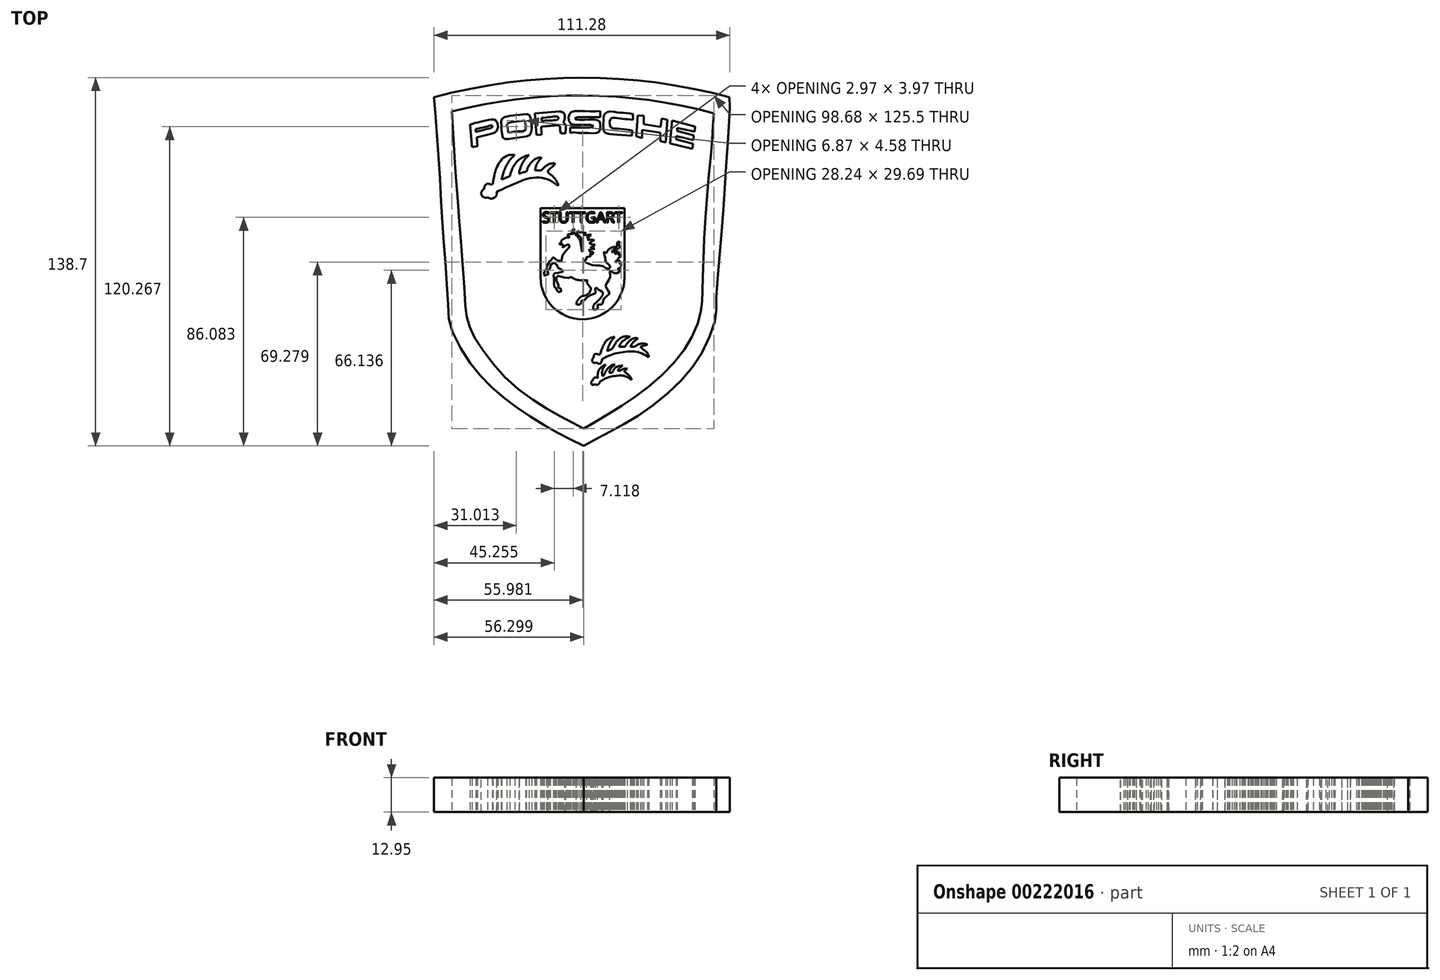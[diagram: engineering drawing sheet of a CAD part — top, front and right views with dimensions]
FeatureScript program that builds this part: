
annotation { "Feature Type Name" : "Feature", "Feature Type Description" : "" }
export const myFeature = defineFeature(function(context is Context, id is Id, definition is map)
    precondition{}
    {
        {
            var Q0;
            Q0=qCreatedBy(makeId("Top.planeOp"),FACE);
            var sketch = newSketch(context, id + "F0", { "sketchPlane" : qUnion([Q0])});
            skFitSpline(sketch, "E0", {"points": [v(35, -72.34) * mm, v(27.57, -68.71) * mm, v(19.8, -64.33) * mm, v(11.03, -58.76) * mm, v(3.44, -53.02) * mm, v(-3.9, -45.93) * mm, v(-10.06, -37.66) * mm, v(-15.16, -27.23) * mm, v(-16.03, -21.12) * mm, v(-16.9, -5.07) * mm, v(-18.13, 10.28) * mm, v(-19.17, 28.25) * mm, v(-20.57, 48.84) * mm, v(-21.37, 59.02) * mm], "startDerivative": vector(-115, 54.33) * mm, "endDerivative": vector(-10.28, 127.52) * mm});
            skArc(sketch, "E1", {"start": v(89.86, 59.02) * mm, "mid": v(34.25, 66.36) * mm, "end": v(-21.37, 59.02) * mm});
            skFitSpline(sketch, "E2", {"points": [v(35, -72.34) * mm, v(45.44, -66.66) * mm, v(56.54, -60.28) * mm, v(70.48, -48.94) * mm, v(79.7, -36.89) * mm, v(84.66, -23.9) * mm, v(84.9, -17.51) * mm, v(86.79, 6.59) * mm, v(88.44, 30.21) * mm, v(89.86, 53.13) * mm, v(89.86, 59.02) * mm], "startDerivative": vector(116.63, 64.03) * mm, "endDerivative": vector(-2, 76.21) * mm});
            skFitSpline(sketch, "E3", {"points": [v(-14.73, 53.62) * mm, v(-13.4, 33.53) * mm, v(-11.42, 6.6) * mm, v(-9.87, -14.37) * mm, v(-9, -24.09) * mm, v(-5.24, -32.92) * mm, v(7.13, -48.15) * mm, v(23.68, -59.85) * mm, v(34.94, -65.81) * mm], "startDerivative": vector(9.08, -141.43) * mm, "endDerivative": vector(98.93, -49.97) * mm});
            skFitSpline(sketch, "E4", {"points": [v(34.94, -65.81) * mm, v(47.97, -58.09) * mm, v(63.64, -46.39) * mm, v(75.56, -31.6) * mm, v(79.32, -20.56) * mm, v(79.76, -13.05) * mm, v(80.64, 11.46) * mm, v(83.07, 40.16) * mm, v(83.95, 52.96) * mm], "startDerivative": vector(107.03, 61.15) * mm, "endDerivative": vector(6.15, 105.05) * mm});
            skArc(sketch, "E5", {"start": v(83.95, 52.96) * mm, "mid": v(34.65, 59.7) * mm, "end": v(-14.73, 53.62) * mm});
            skFitSpline(sketch, "E6.0", {"points": [v(-11.94, 53.8) * mm, v(-11.75, 50.85) * mm, v(-11.47, 46.44) * mm, v(-11.07, 40.3) * mm, v(-10.8, 36.31) * mm, v(-10.57, 33) * mm, v(-10.33, 29.59) * mm, v(-10.02, 25.2) * mm, v(-9.62, 19.8) * mm, v(-9.22, 14.33) * mm, v(-8.8, 8.9) * mm, v(-8.38, 3.58) * mm, v(-7.97, -1.55) * mm, v(-7.6, -6.4) * mm, v(-7.33, -10.14) * mm, v(-7.16, -12.9) * mm, v(-7.05, -14.86) * mm, v(-6.96, -16.65) * mm, v(-6.85, -18.86) * mm, v(-6.7, -20.81) * mm, v(-6.45, -22.57) * mm, v(-6.2, -23.82) * mm, v(-5.87, -25.05) * mm, v(-5.3, -26.7) * mm, v(-4.54, -28.44) * mm, v(-3.52, -30.34) * mm, v(-2.63, -31.86) * mm, v(-1.6, -33.48) * mm, v(-0.08, -35.73) * mm, v(2.1, -38.66) * mm, v(5.1, -42.2) * mm, v(7.85, -45.04) * mm, v(10.16, -47.15) * mm, v(12.56, -49.17) * mm, v(15.67, -51.52) * mm, v(19.45, -54.07) * mm, v(22.56, -55.97) * mm, v(24.95, -57.36) * mm, v(27.25, -58.66) * mm, v(29.98, -60.14) * mm, v(33.12, -61.76) * mm, v(35.17, -62.8) * mm, v(36.2, -63.32) * mm]});
            skArc(sketch, "E6.1", {"start": v(81.03, 50.84) * mm, "mid": v(34.66, 56.9) * mm, "end": v(-11.8, 51.48) * mm});
            skFitSpline(sketch, "E6.2", {"points": [v(33.56, -63.39) * mm, v(35.79, -62.11) * mm, v(39.11, -60.21) * mm, v(43.08, -57.84) * mm, v(45.4, -56.4) * mm, v(47.75, -54.92) * mm, v(50.74, -52.96) * mm, v(54.35, -50.41) * mm, v(57.92, -47.68) * mm, v(60.78, -45.24) * mm, v(62.98, -43.2) * mm, v(65.1, -41.08) * mm, v(67.6, -38.33) * mm, v(70.24, -34.96) * mm, v(72.09, -32.14) * mm, v(73.3, -29.92) * mm, v(74.1, -28.27) * mm, v(74.78, -26.64) * mm, v(75.35, -25.04) * mm, v(75.81, -23.5) * mm, v(76.19, -22.05) * mm, v(76.42, -20.9) * mm, v(76.57, -20.05) * mm, v(76.7, -19.23) * mm, v(76.8, -18.26) * mm, v(76.88, -17.08) * mm, v(76.92, -15.82) * mm, v(76.94, -14.63) * mm, v(76.96, -13.56) * mm, v(76.97, -12.42) * mm, v(77, -10.83) * mm, v(77.03, -8.72) * mm, v(77.1, -5.64) * mm, v(77.23, -1.38) * mm, v(77.44, 4.22) * mm, v(77.7, 9.14) * mm, v(77.95, 13.12) * mm, v(78.23, 17.11) * mm, v(78.63, 22.07) * mm, v(79.14, 27.82) * mm, v(79.56, 32.35) * mm, v(79.87, 35.75) * mm, v(80.1, 38.16) * mm, v(80.3, 40.43) * mm, v(80.46, 42.53) * mm, v(80.61, 44.5) * mm, v(80.79, 46.98) * mm, v(80.97, 49.85) * mm, v(81.1, 52.03) * mm, v(81.16, 53.12) * mm]});
            skLineSegment(sketch, "E7", {"start": v(-9.6, 50.21) * mm, "end": v(-8.62, 38.48) * mm});
            skArc(sketch, "E8", {"start": v(78.46, 49.18) * mm, "mid": v(34.5, 55.61) * mm, "end": v(-9.6, 50.21) * mm});
            skArc(sketch, "E9", {"start": v(77.32, 37.5) * mm, "mid": v(34.41, 43.44) * mm, "end": v(-8.62, 38.48) * mm});
            skLineSegment(sketch, "E10", {"start": v(78.46, 49.18) * mm, "end": v(77.32, 37.5) * mm});
            skLineSegment(sketch, "E11", {"start": v(35.61, 31.18) * mm, "end": v(35.61, 19.11) * mm});
            skLineSegment(sketch, "E12", {"start": v(35.61, 19.11) * mm, "end": v(76.07, 19.11) * mm});
            skLineSegment(sketch, "E13", {"start": v(76.07, 19.11) * mm, "end": v(77.32, 31.18) * mm});
            skLineSegment(sketch, "E14", {"start": v(77.32, 31.18) * mm, "end": v(35.61, 31.18) * mm});
            skLineSegment(sketch, "E15", {"start": v(52.26, 5.93) * mm, "end": v(52.26, -6.08) * mm});
            skLineSegment(sketch, "E16", {"start": v(52.26, -6.08) * mm, "end": v(74.52, -6.08) * mm});
            skLineSegment(sketch, "E17", {"start": v(74.52, -6.08) * mm, "end": v(75.38, 5.93) * mm});
            skLineSegment(sketch, "E18", {"start": v(75.38, 5.93) * mm, "end": v(52.26, 5.93) * mm});
            skFitSpline(sketch, "E19", {"points": [v(0.8, 26.31) * mm, v(1.4, 30.07) * mm, v(3.4, 34.67) * mm, v(6.46, 37.12) * mm, v(9.07, 37.27) * mm], "startDerivative": vector(1.67, 14.46) * mm, "endDerivative": vector(12.44, -1) * mm});
            skFitSpline(sketch, "E20", {"points": [v(9.07, 37.27) * mm, v(6.85, 34.9) * mm, v(4.93, 31.07) * mm, v(4.09, 28) * mm], "startDerivative": vector(-7.23, -6.64) * mm, "endDerivative": vector(-2.15, -9.34) * mm});
            skFitSpline(sketch, "E21", {"points": [v(4.09, 28) * mm, v(7.23, 29.3) * mm], "startDerivative": vector(3.14, 1.3) * mm, "endDerivative": vector(3.14, 1.3) * mm});
            skFitSpline(sketch, "E22", {"points": [v(7.23, 29.3) * mm, v(8.46, 32.83) * mm, v(11.3, 35.97) * mm, v(14.43, 37.27) * mm], "startDerivative": vector(2.7, 10.77) * mm, "endDerivative": vector(10.14, 3.02) * mm});
            skFitSpline(sketch, "E23", {"points": [v(14.43, 37.27) * mm, v(12.29, 34.82) * mm, v(10.76, 31.07) * mm, v(10.76, 30.15) * mm], "startDerivative": vector(-5.9, -5.48) * mm, "endDerivative": vector(0.55, -3.7) * mm});
            skFitSpline(sketch, "E24", {"points": [v(10.76, 30.15) * mm, v(12.36, 30.76) * mm, v(13.44, 30.91) * mm], "startDerivative": vector(3.01, 1.3) * mm, "endDerivative": vector(2.32, 0.18) * mm});
            skFitSpline(sketch, "E25", {"points": [v(13.44, 30.91) * mm, v(14.43, 33.37) * mm, v(17.35, 36.05) * mm, v(19.1, 36.2) * mm], "startDerivative": vector(1.95, 7.2) * mm, "endDerivative": vector(6.15, -0.71) * mm});
            skFitSpline(sketch, "E26", {"points": [v(19.1, 36.2) * mm, v(17.8, 34.67) * mm, v(16.96, 32.83) * mm, v(16.7, 31.46) * mm], "startDerivative": vector(-3.94, -4.08) * mm, "endDerivative": vector(-0.64, -4.47) * mm});
            skFitSpline(sketch, "E27", {"points": [v(16.7, 31.46) * mm, v(19.1, 31.46) * mm], "startDerivative": vector(2.42, 0) * mm, "endDerivative": vector(2.42, 0) * mm});
            skFitSpline(sketch, "E28", {"points": [v(19.1, 31.46) * mm, v(20.67, 33.08) * mm, v(22.43, 33.96) * mm, v(24.35, 34.01) * mm], "startDerivative": vector(4.24, 4.99) * mm, "endDerivative": vector(6.01, -0.4) * mm});
            skFitSpline(sketch, "E29", {"points": [v(24.35, 34.01) * mm, v(22.58, 32.3) * mm, v(21.5, 30.91) * mm, v(23.22, 29.3) * mm, v(25.03, 26.9) * mm, v(25.47, 25.58) * mm], "startDerivative": vector(-7.92, -8.09) * mm, "endDerivative": vector(1.93, -7.65) * mm});
            skFitSpline(sketch, "E30", {"points": [v(25.47, 25.58) * mm, v(22.48, 27.54) * mm, v(19.1, 28.62) * mm, v(14.43, 28.42) * mm, v(9.07, 26.46) * mm, v(4.09, 24.25) * mm, v(2.22, 23.32) * mm], "startDerivative": vector(-18.76, 13.66) * mm, "endDerivative": vector(-13.58, -7.08) * mm});
            skFitSpline(sketch, "E31", {"points": [v(2.22, 23.32) * mm, v(2.22, 22.34) * mm, v(1.49, 21.26) * mm, v(0, 20.82) * mm, v(-1.21, 21.26) * mm], "startDerivative": vector(0.56, -4.4) * mm, "endDerivative": vector(-4.55, 2.43) * mm});
            skFitSpline(sketch, "E32", {"points": [v(-1.21, 21.26) * mm, v(-2.54, 21.26) * mm, v(-3.57, 22.34) * mm, v(-3.37, 23.6) * mm, v(-2.58, 24.45) * mm, v(-2.24, 25.58) * mm, v(-1.21, 26.46) * mm, v(0, 26.16) * mm, v(0.8, 26.31) * mm], "startDerivative": vector(-10.36, -1.82) * mm, "endDerivative": vector(7.37, 2.91) * mm});
            skLineSegment(sketch, "E33", {"start": v(33.17, 19.11) * mm, "end": v(33.17, 41.97) * mm});
            skLineSegment(sketch, "E34", {"start": v(16.5, 19.11) * mm, "end": v(33.17, 19.11) * mm});
            skLineSegment(sketch, "E35", {"start": v(16.5, 19.11) * mm, "end": v(16.5, 17.4) * mm});
            skLineSegment(sketch, "E36", {"start": v(16.5, 14.72) * mm, "end": v(16.5, 7.66) * mm});
            skLineSegment(sketch, "E37", {"start": v(17.06, 6.18) * mm, "end": v(17.06, 4.03) * mm});
            skLineSegment(sketch, "E38", {"start": v(17.06, 4.03) * mm, "end": v(15.66, 4.48) * mm});
            skLineSegment(sketch, "E39", {"start": v(15.66, 4.48) * mm, "end": v(17.06, 6.18) * mm});
            skLineSegment(sketch, "E40", {"start": v(17.06, 1.93) * mm, "end": v(17.06, -6.32) * mm});
            skLineSegment(sketch, "E41", {"start": v(17.06, -6.32) * mm, "end": v(-6.18, -6.32) * mm});
            skLineSegment(sketch, "E42", {"start": v(-6.18, -6.32) * mm, "end": v(-8.79, 36.4) * mm});
            skArc(sketch, "E43", {"start": v(33.17, 41.97) * mm, "mid": v(12.03, 40.4) * mm, "end": v(-8.79, 36.4) * mm});
            skArc(sketch, "E44", {"start": v(-4.38, -19.17) * mm, "mid": v(-3.07, -25.62) * mm, "end": v(0, -31.44) * mm});
            skArc(sketch, "E45", {"start": v(19.45, -19.17) * mm, "mid": v(25.5, -24.57) * mm, "end": v(33.17, -27.26) * mm});
            skLineSegment(sketch, "E46", {"start": v(-4.38, -19.17) * mm, "end": v(19.45, -19.17) * mm});
            skLineSegment(sketch, "E47", {"start": v(0, -31.44) * mm, "end": v(33.17, -31.44) * mm});
            skLineSegment(sketch, "E48", {"start": v(33.17, -31.44) * mm, "end": v(33.17, -27.26) * mm});
            skLineSegment(sketch, "E49", {"start": v(11.01, -44.51) * mm, "end": v(33.27, -44.51) * mm});
            skLineSegment(sketch, "E50", {"start": v(33.27, -44.51) * mm, "end": v(33.27, -59.66) * mm});
            skArc(sketch, "E51", {"start": v(11.01, -44.51) * mm, "mid": v(21.66, -52.8) * mm, "end": v(33.27, -59.66) * mm});
            skLineSegment(sketch, "E52", {"start": v(35.56, -26.74) * mm, "end": v(35.56, -59.86) * mm});
            skArc(sketch, "E53", {"start": v(35.56, -26.74) * mm, "mid": v(39.29, -26.2) * mm, "end": v(42.79, -24.83) * mm});
            skArc(sketch, "E54", {"start": v(45.23, -23.38) * mm, "mid": v(50.72, -16.77) * mm, "end": v(52.26, -8.32) * mm});
            skLineSegment(sketch, "E55", {"start": v(52.26, -8.32) * mm, "end": v(74.52, -8.32) * mm});
            skFitSpline(sketch, "E56", {"points": [v(35.56, -59.86) * mm, v(46.42, -53.55) * mm, v(60.92, -42.5) * mm, v(70.52, -29.8) * mm, v(73.6, -19.66) * mm, v(74.52, -8.32) * mm], "startDerivative": vector(54.2, 29.95) * mm, "endDerivative": vector(3.1, 63.4) * mm});
            skLineSegment(sketch, "E57", {"start": v(18.72, 17.2) * mm, "end": v(50.36, 17.2) * mm});
            skLineSegment(sketch, "E58", {"start": v(18.72, 17.2) * mm, "end": v(18.72, -2.86) * mm});
            skLineSegment(sketch, "E59", {"start": v(50.36, 17.2) * mm, "end": v(50.36, -2.86) * mm});
            skLineSegment(sketch, "E60", {"start": v(18.72, -2.86) * mm, "end": v(18.72, -8.82) * mm});
            skLineSegment(sketch, "E61", {"start": v(50.36, -2.86) * mm, "end": v(50.36, -8.82) * mm});
            skArc(sketch, "E62", {"start": v(18.72, -8.82) * mm, "mid": v(34.54, -24.64) * mm, "end": v(50.36, -8.82) * mm});
            skLineSegment(sketch, "E63", {"start": v(16.5, 17.4) * mm, "end": v(15.06, 17.4) * mm});
            skFitSpline(sketch, "E64", {"points": [v(15.06, 17.4) * mm, v(15.83, 18.96) * mm, v(17.27, 20.5) * mm, v(18.01, 21.29) * mm], "startDerivative": vector(1.78, 4.5) * mm, "endDerivative": vector(2.4, 2.6) * mm});
            skFitSpline(sketch, "E65", {"points": [v(18.01, 21.29) * mm, v(16.42, 21.29) * mm, v(14.13, 19.47) * mm, v(12.9, 17.4) * mm], "startDerivative": vector(-5.47, 1.03) * mm, "endDerivative": vector(-2.9, -6) * mm});
            skFitSpline(sketch, "E66", {"points": [v(12.9, 17.4) * mm, v(10.36, 16.77) * mm], "startDerivative": vector(-2.55, -0.63) * mm, "endDerivative": vector(-2.55, -0.63) * mm});
            skFitSpline(sketch, "E67", {"points": [v(10.36, 16.77) * mm, v(10.73, 18.18) * mm, v(11.95, 20.32) * mm, v(13.87, 22.32) * mm], "startDerivative": vector(0.97, 4.93) * mm, "endDerivative": vector(5.43, 5.06) * mm});
            skFitSpline(sketch, "E68", {"points": [v(13.87, 22.32) * mm, v(12.28, 22.32) * mm, v(9.7, 20.58) * mm, v(7.66, 17.4) * mm, v(7.25, 15.66) * mm], "startDerivative": vector(-7.6, 1.12) * mm, "endDerivative": vector(-1.06, -7.6) * mm});
            skFitSpline(sketch, "E69", {"points": [v(7.25, 15.66) * mm, v(4.5, 14.86) * mm], "startDerivative": vector(-2.76, -0.8) * mm, "endDerivative": vector(-2.76, -0.8) * mm});
            skFitSpline(sketch, "E70", {"points": [v(4.5, 14.86) * mm, v(5.2, 17.38) * mm, v(6.42, 19.47) * mm, v(8.95, 22.32) * mm], "startDerivative": vector(1.9, 8.32) * mm, "endDerivative": vector(7.25, 7.74) * mm});
            skFitSpline(sketch, "E71", {"points": [v(8.95, 22.32) * mm, v(6.66, 22.32) * mm, v(3.79, 19.47) * mm, v(2.38, 16.62) * mm, v(1.97, 13.57) * mm], "startDerivative": vector(-10.58, 2.26) * mm, "endDerivative": vector(-0.9, -12.63) * mm});
            skFitSpline(sketch, "E72", {"points": [v(1.97, 13.57) * mm, v(1.97, 13.1) * mm, v(0.74, 13.57) * mm, v(-0.78, 13.57) * mm, v(-1.43, 12.34) * mm, v(-2.13, 11.17) * mm, v(-2.13, 9.53) * mm, v(-0.96, 8.7) * mm, v(0.62, 8.88) * mm, v(1.97, 8.53) * mm, v(3.03, 9.58) * mm, v(3.14, 10.93) * mm], "startDerivative": vector(2.53, -11.61) * mm, "endDerivative": vector(-1.04, 14.53) * mm});
            skFitSpline(sketch, "E73", {"points": [v(3.14, 10.93) * mm, v(7.07, 12.98) * mm, v(12.34, 14.74) * mm, v(16.5, 14.72) * mm], "startDerivative": vector(11.43, 6.38) * mm, "endDerivative": vector(12.78, -1.19) * mm});
            skFitSpline(sketch, "E74", {"points": [v(16.5, 7.66) * mm, v(15.02, 6.83) * mm, v(13.46, 5) * mm], "startDerivative": vector(-3.33, -1.46) * mm, "endDerivative": vector(-2.76, -3.78) * mm});
            skFitSpline(sketch, "E75", {"points": [v(13.46, 5) * mm, v(11.9, 5) * mm], "startDerivative": vector(-1.56, 0) * mm, "endDerivative": vector(-1.56, 0) * mm});
            skFitSpline(sketch, "E76", {"points": [v(11.9, 5) * mm, v(12.34, 6.34) * mm, v(13.46, 8.25) * mm], "startDerivative": vector(0.76, 2.91) * mm, "endDerivative": vector(2.3, 3.55) * mm});
            skFitSpline(sketch, "E77", {"points": [v(13.46, 8.25) * mm, v(12.34, 8.25) * mm, v(10.93, 6.74) * mm, v(9.69, 4.25) * mm], "startDerivative": vector(-4.42, 0.9) * mm, "endDerivative": vector(-2.85, -6.38) * mm});
            skFitSpline(sketch, "E78", {"points": [v(9.69, 4.25) * mm, v(8.09, 4.25) * mm], "startDerivative": vector(-1.6, 0) * mm, "endDerivative": vector(-1.6, 0) * mm});
            skFitSpline(sketch, "E79", {"points": [v(8.09, 4.25) * mm, v(8.53, 5.72) * mm, v(9.6, 7.5) * mm, v(10.3, 8.34) * mm], "startDerivative": vector(0.96, 4.25) * mm, "endDerivative": vector(2.38, 2.62) * mm});
            skFitSpline(sketch, "E80", {"points": [v(10.3, 8.34) * mm, v(8.09, 7.9) * mm, v(6.84, 6.2) * mm, v(6, 4.25) * mm, v(5.9, 2.83) * mm], "startDerivative": vector(-9.16, -0.41) * mm, "endDerivative": vector(0.22, -6.5) * mm});
            skFitSpline(sketch, "E81", {"points": [v(5.9, 2.83) * mm, v(3.82, 1.8) * mm], "startDerivative": vector(-2.09, -1.02) * mm, "endDerivative": vector(-2.09, -1.02) * mm});
            skFitSpline(sketch, "E82", {"points": [v(3.82, 1.8) * mm, v(3.82, 3.27) * mm, v(4.75, 5.9) * mm, v(5.9, 7.72) * mm], "startDerivative": vector(-0.5, 4.82) * mm, "endDerivative": vector(3.5, 4.91) * mm});
            skFitSpline(sketch, "E83", {"points": [v(5.9, 7.72) * mm, v(4.4, 7) * mm, v(2.57, 4.7) * mm, v(1.77, 1.8) * mm, v(1.77, 0) * mm, v(0.93, 0) * mm, v(-0.58, -0.37) * mm, v(-0.85, -1.75) * mm, v(-1.11, -2.64) * mm, v(-0.71, -3.8) * mm, v(0.57, -3.84) * mm, v(1.9, -4.02) * mm, v(2.93, -3.26) * mm, v(2.89, -2.06) * mm], "startDerivative": vector(-18.75, -6.14) * mm, "endDerivative": vector(-4.43, 18.3) * mm});
            skFitSpline(sketch, "E84", {"points": [v(2.89, -2.06) * mm, v(6.49, 0.74) * mm, v(9.82, 2.3) * mm, v(13.73, 2.83) * mm, v(17.06, 1.93) * mm], "startDerivative": vector(13.36, 11.26) * mm, "endDerivative": vector(13.67, -5.14) * mm});
            skLineSegment(sketch, "E85", {"start": v(42.79, -24.83) * mm, "end": v(42.79, -27.24) * mm});
            skLineSegment(sketch, "E86", {"start": v(45.23, -23.38) * mm, "end": v(45.23, -26.36) * mm});
            skLineSegment(sketch, "E87", {"start": v(45.23, -26.36) * mm, "end": v(46.71, -25.9) * mm});
            skFitSpline(sketch, "E88", {"points": [v(46.71, -25.9) * mm, v(48.5, -22.78) * mm, v(51.13, -20.43) * mm, v(54.44, -19.56) * mm], "startDerivative": vector(4.78, 9.56) * mm, "endDerivative": vector(10.47, 1.64) * mm});
            skFitSpline(sketch, "E89", {"points": [v(54.44, -19.56) * mm, v(51.86, -21.72) * mm, v(50.2, -24.52) * mm], "startDerivative": vector(-5.55, -3.94) * mm, "endDerivative": vector(-2.9, -6) * mm});
            skFitSpline(sketch, "E90", {"points": [v(50.2, -24.52) * mm, v(53.06, -24.52) * mm], "startDerivative": vector(2.85, 0) * mm, "endDerivative": vector(2.85, 0) * mm});
            skFitSpline(sketch, "E91", {"points": [v(53.06, -24.52) * mm, v(54.44, -22.55) * mm, v(56.78, -20.66) * mm, v(59.17, -20.66) * mm], "startDerivative": vector(3.79, 6.03) * mm, "endDerivative": vector(7.56, -1.27) * mm});
            skFitSpline(sketch, "E92", {"points": [v(59.17, -20.66) * mm, v(57.47, -21.72) * mm, v(56.1, -24.06) * mm], "startDerivative": vector(-3.94, -1.81) * mm, "endDerivative": vector(-2.26, -4.91) * mm});
            skFitSpline(sketch, "E93", {"points": [v(56.1, -24.06) * mm, v(57.56, -24.06) * mm, v(59.17, -23.56) * mm, v(61.2, -22.78) * mm, v(63.86, -23.38) * mm], "startDerivative": vector(6.83, -0.44) * mm, "endDerivative": vector(9.42, -3.48) * mm});
            skFitSpline(sketch, "E94", {"points": [v(63.86, -23.38) * mm, v(61.8, -23.78) * mm, v(60.7, -24.52) * mm], "startDerivative": vector(-4.04, -0.45) * mm, "endDerivative": vector(-2.2, -1.9) * mm});
            skFitSpline(sketch, "E95", {"points": [v(60.7, -24.52) * mm, v(63.05, -25.9) * mm, v(64.62, -28.56) * mm, v(64.56, -30.86) * mm], "startDerivative": vector(7.35, -3.25) * mm, "endDerivative": vector(-1.17, -7.24) * mm});
            skFitSpline(sketch, "E96", {"points": [v(64.56, -30.86) * mm, v(62.75, -28.68) * mm, v(59.85, -27) * mm, v(56.1, -26.51) * mm, v(50.2, -27.48) * mm, v(45.73, -29.05) * mm, v(42.53, -30.86) * mm], "startDerivative": vector(-11.54, 16.21) * mm, "endDerivative": vector(-19.22, -11.87) * mm});
            skFitSpline(sketch, "E97", {"points": [v(42.53, -30.86) * mm, v(42.05, -31.82) * mm, v(40.66, -32) * mm, v(39.57, -32.06) * mm, v(38.48, -31.64) * mm, v(38.42, -30.86) * mm, v(38.73, -29.83) * mm, v(38.85, -28.62) * mm, v(39.7, -27.78) * mm, v(41.14, -28.14) * mm, v(41.99, -28.02) * mm, v(42.79, -27.24) * mm], "startDerivative": vector(-3.18, -13.12) * mm, "endDerivative": vector(8.56, 10.1) * mm});
            skFitSpline(sketch, "E98", {"points": [v(30.18, -8.63) * mm, v(29.52, -9) * mm, v(28.07, -9) * mm, v(26.19, -8.5) * mm, v(25.4, -8.27) * mm, v(24.77, -8.6) * mm, v(24.7, -9.53) * mm, v(24.73, -10.48) * mm, v(25.13, -10.88) * mm, v(25.43, -11.7) * mm, v(25.43, -12.8) * mm, v(26.12, -12.86) * mm, v(26.48, -13.56) * mm, v(26.22, -14.51) * mm, v(25.26, -14.28) * mm, v(24.77, -13.62) * mm, v(24.67, -13.1) * mm, v(24.14, -12.7) * mm, v(23.87, -12.2) * mm, v(23.84, -11.28) * mm, v(23.84, -10.19) * mm, v(23.84, -8.96) * mm, v(23.64, -8.54) * mm, v(23.64, -7.51) * mm, v(24.5, -7.25) * mm, v(25.7, -7.05) * mm, v(26.62, -6.79) * mm, v(27.3, -6.52) * mm], "startDerivative": vector(-17.28, -12.58) * mm, "endDerivative": vector(19.86, 7.98) * mm});
            skFitSpline(sketch, "E99", {"points": [v(27.3, -6.52) * mm, v(26.95, -6.03) * mm, v(26.42, -5.83) * mm, v(25.79, -5.9) * mm, v(25.43, -5.4) * mm, v(25.03, -4.9) * mm, v(24.9, -4.14) * mm, v(24.5, -3.62) * mm, v(23.84, -3.35) * mm, v(23.15, -3.45) * mm, v(22.65, -3.98) * mm, v(22.52, -4.8) * mm, v(22.1, -5.7) * mm, v(21.53, -6.1) * mm, v(21.46, -6.52) * mm, v(21.83, -7.25) * mm, v(21.27, -7.97) * mm, v(20.5, -8.17) * mm, v(19.94, -8.1) * mm, v(19.94, -7.35) * mm, v(20.18, -6.52) * mm, v(20.7, -6.2) * mm, v(20.84, -5.17) * mm, v(21.5, -4.01) * mm, v(22.39, -2.62) * mm, v(23.28, -1.37) * mm, v(24.14, -1.53) * mm, v(25.5, -2.72) * mm, v(26.48, -2.82) * mm, v(26.78, -1.34) * mm, v(27.3, 0) * mm, v(28.66, 1.44) * mm, v(29.59, 2.53) * mm, v(29.82, 3.29) * mm, v(29.2, 3.62) * mm, v(28.63, 3.55) * mm, v(28.07, 3.02) * mm, v(27.6, 2.46) * mm, v(27.01, 2.43) * mm, v(26.98, 2.99) * mm, v(27.3, 3.52) * mm], "startDerivative": vector(-15.27, 25.76) * mm, "endDerivative": vector(18.12, 22.34) * mm});
            skFitSpline(sketch, "E100", {"points": [v(27.3, 3.52) * mm, v(25.96, 3.52) * mm], "startDerivative": vector(-1.35, 0) * mm, "endDerivative": vector(-1.35, 0) * mm});
            skFitSpline(sketch, "E101", {"points": [v(25.96, 3.52) * mm, v(25.96, 4) * mm, v(26.4, 4.05) * mm, v(26.4, 4.59) * mm, v(27.3, 5.55) * mm, v(28.34, 6.13) * mm, v(29.3, 6.13) * mm, v(29.61, 6.47) * mm, v(29, 6.74) * mm, v(28.96, 7.24) * mm, v(30, 7.43) * mm, v(31.15, 7.63) * mm, v(31.84, 8) * mm], "startDerivative": vector(-2.52, 9.7) * mm, "endDerivative": vector(7.6, 5.07) * mm});
            skFitSpline(sketch, "E102", {"points": [v(31.84, 8) * mm, v(31.84, 7.24) * mm], "startDerivative": vector(0, -0.77) * mm, "endDerivative": vector(0, -0.77) * mm});
            skFitSpline(sketch, "E103", {"points": [v(31.84, 7.24) * mm, v(33.11, 5.93) * mm, v(33.77, 4.28) * mm, v(34.35, 0.66) * mm], "startDerivative": vector(4.82, -4.29) * mm, "endDerivative": vector(1.28, -9.52) * mm});
            skFitSpline(sketch, "E104", {"points": [v(34.35, 0.66) * mm, v(34.65, 2.82) * mm, v(34.35, 5.16) * mm, v(33.23, 6.82) * mm, v(32.54, 7.5) * mm, v(32.65, 8.4) * mm, v(33.11, 8.63) * mm, v(33.23, 8) * mm], "startDerivative": vector(2.16, 11.26) * mm, "endDerivative": vector(-0.1, -8.16) * mm});
            skFitSpline(sketch, "E105", {"points": [v(33.23, 8) * mm, v(34.35, 8) * mm, v(35.73, 8) * mm, v(35.2, 7.5) * mm, v(34.96, 6.93) * mm, v(36.38, 7.24) * mm, v(37.77, 7.24) * mm, v(37.35, 6.74) * mm, v(36.5, 6.55) * mm, v(36.23, 6.13) * mm, v(36.92, 5.86) * mm, v(36.54, 5.4) * mm, v(37.61, 5.28) * mm, v(38.42, 5.47) * mm, v(38.88, 5.09) * mm, v(37.88, 4.66) * mm, v(37.11, 4.24) * mm, v(37.42, 3.82) * mm, v(38.42, 3.52) * mm, v(39.04, 3.52) * mm, v(39.08, 2.86) * mm, v(38.04, 2.74) * mm, v(37.58, 2.4) * mm, v(38.42, 2.36) * mm, v(39, 2.2) * mm, v(38.85, 1.7) * mm, v(37.92, 1.66) * mm, v(36.96, 1.55) * mm, v(37.38, 1.2) * mm, v(37.46, 0.66) * mm, v(38.58, 0.66) * mm], "startDerivative": vector(23.89, -1.07) * mm, "endDerivative": vector(38.45, 6.6) * mm});
            skFitSpline(sketch, "E106", {"points": [v(38.58, 0.66) * mm, v(38.58, 0) * mm, v(37.38, 0) * mm, v(37.61, -0.57) * mm, v(37.27, -1.15) * mm, v(36.04, -1.03) * mm, v(36.15, -1.91) * mm, v(35.27, -2.15) * mm, v(35.2, -2.72) * mm, v(36.61, -3.6) * mm, v(38.58, -4.3) * mm, v(40.3, -4.34) * mm, v(42.3, -4.68) * mm, v(43.73, -5.57) * mm, v(44.85, -5.45) * mm, v(44.89, -4.57) * mm, v(43.88, -3.6) * mm, v(43.2, -2.65) * mm, v(43.2, -1.8) * mm, v(42.88, -0.76) * mm, v(42.62, 0.66) * mm, v(43.5, 0.32) * mm], "startDerivative": vector(8.18, -23.64) * mm, "endDerivative": vector(26.26, -16.63) * mm});
            skFitSpline(sketch, "E107", {"points": [v(43.5, 0.32) * mm, v(44.38, 1.66) * mm, v(45.89, 2.5) * mm, v(47.5, 2.7) * mm], "startDerivative": vector(2.27, 4.39) * mm, "endDerivative": vector(4.9, 0.19) * mm});
            skFitSpline(sketch, "E108", {"points": [v(47.5, 2.7) * mm, v(47.5, 3.52) * mm, v(47.78, 4.46) * mm, v(48.35, 4.6) * mm, v(48.25, 3.96) * mm, v(48.13, 3.52) * mm, v(48.47, 2.7) * mm, v(48.2, 2.06) * mm, v(47.04, 2.03) * mm, v(46.02, 1.44) * mm, v(45.65, 0.66) * mm, v(46.1, 0.66) * mm, v(46.74, 1.21) * mm, v(47.5, 1.44) * mm, v(47.78, 1.39) * mm], "startDerivative": vector(-0.25, 10.28) * mm, "endDerivative": vector(5.35, -1.65) * mm});
            skFitSpline(sketch, "E109", {"points": [v(47.78, 1.39) * mm, v(47.28, 1) * mm, v(46.8, 0.44) * mm, v(46.86, 0) * mm, v(47.48, 0.22) * mm, v(48.24, 0.54) * mm, v(48.53, 0.41) * mm], "startDerivative": vector(-2.8, -2.11) * mm, "endDerivative": vector(2.11, -1.57) * mm});
            skFitSpline(sketch, "E110", {"points": [v(48.53, 0.41) * mm, v(48.16, 0.13) * mm, v(48, -0.26) * mm, v(48.38, -0.36) * mm, v(48.97, -0.44) * mm, v(48.98, -0.93) * mm, v(48.4, -1.31) * mm, v(47.88, -1.82) * mm, v(47.78, -2.41) * mm], "startDerivative": vector(-3.41, -1.95) * mm, "endDerivative": vector(-0.17, -4.64) * mm});
            skFitSpline(sketch, "E111", {"points": [v(47.78, -2.41) * mm, v(47.18, -2.55) * mm, v(47.03, -3.1) * mm, v(47.59, -2.92) * mm, v(48.24, -2.63) * mm, v(48.65, -2.61) * mm], "startDerivative": vector(-3.27, 0.15) * mm, "endDerivative": vector(2.36, -0.08) * mm});
            skFitSpline(sketch, "E112", {"points": [v(48.65, -2.61) * mm, v(48.65, -2.86) * mm, v(48.47, -3.6) * mm, v(48.98, -3.6) * mm, v(49.05, -4.7) * mm, v(48.16, -5.57) * mm, v(47.78, -5.57) * mm, v(48.47, -6.08) * mm, v(48.47, -6.52) * mm, v(47.78, -7.22) * mm, v(46.4, -7.15) * mm, v(44.87, -6.52) * mm, v(44.77, -7.05) * mm, v(44.97, -8.05) * mm, v(44.57, -9.6) * mm, v(43.46, -11.36) * mm, v(43.3, -12.3) * mm, v(44.13, -13.84) * mm, v(44.67, -14.6) * mm], "startDerivative": vector(1.76, -6.49) * mm, "endDerivative": vector(8.61, -12.19) * mm});
            skFitSpline(sketch, "E113", {"points": [v(30.18, -8.63) * mm, v(31.8, -9.6) * mm, v(34.13, -9.96) * mm, v(36.5, -9.96) * mm], "startDerivative": vector(4.86, -3.57) * mm, "endDerivative": vector(6.75, 0.13) * mm});
            skFitSpline(sketch, "E114", {"points": [v(36.5, -9.96) * mm, v(36.13, -10.8) * mm, v(37.22, -12.22) * mm, v(37.68, -13.2) * mm, v(37.02, -14.69) * mm, v(35.5, -15.7) * mm, v(34.32, -15.93) * mm, v(32.98, -17.05) * mm, v(32.29, -18.36) * mm, v(32.26, -19.09) * mm], "startDerivative": vector(-6.9, -8.73) * mm, "endDerivative": vector(0.56, -8.33) * mm});
            skFitSpline(sketch, "E115", {"points": [v(32.26, -19.09) * mm, v(33.3, -19.09) * mm, v(34.06, -18.53) * mm], "startDerivative": vector(2.17, -0.3) * mm, "endDerivative": vector(1.43, 1.43) * mm});
            skFitSpline(sketch, "E116", {"points": [v(34.06, -18.53) * mm, v(34.06, -17.84) * mm, v(34.42, -17.58) * mm, v(35.24, -17.48) * mm, v(36, -16.57) * mm, v(38.22, -15.29) * mm, v(39.36, -14.76) * mm, v(39.36, -13.29) * mm, v(39.7, -12.73) * mm, v(40.51, -13.49) * mm, v(41.75, -14.17) * mm, v(42.28, -14.9) * mm, v(41.56, -16.3) * mm, v(40.51, -17.48) * mm, v(39.07, -18.83) * mm], "startDerivative": vector(-1.96, 14.22) * mm, "endDerivative": vector(-16.63, -15.07) * mm});
            skFitSpline(sketch, "E117", {"points": [v(39.07, -18.83) * mm, v(38.6, -19.75) * mm, v(38.5, -21) * mm], "startDerivative": vector(-1.17, -1.84) * mm, "endDerivative": vector(0, -2.5) * mm});
            skFitSpline(sketch, "E118", {"points": [v(38.5, -21) * mm, v(39.5, -21) * mm, v(40.38, -20.43) * mm], "startDerivative": vector(2.1, -0.28) * mm, "endDerivative": vector(1.69, 1.4) * mm});
            skFitSpline(sketch, "E119", {"points": [v(40.38, -20.43) * mm, v(40.17, -19.71) * mm, v(40.38, -19.09) * mm, v(41.52, -19.09) * mm, v(42.24, -18.18) * mm, v(42.52, -17.05) * mm, v(44.23, -15.4) * mm, v(44.67, -14.6) * mm], "startDerivative": vector(-2.45, 5.76) * mm, "endDerivative": vector(1.93, 5.8) * mm});
            skFitSpline(sketch, "E120", {"points": [v(30.18, 8.36) * mm, v(31.3, 9.31) * mm, v(31.31, 8.86) * mm, v(31.21, 8.36) * mm, v(30.79, 8.35) * mm, v(30.18, 8.36) * mm]});
            skFitSpline(sketch, "E121", {"points": [v(41.16, -37.73) * mm, v(42.55, -34.17) * mm, v(44.32, -32.05) * mm, v(46.7, -31.26) * mm], "startDerivative": vector(3.3, 9.98) * mm, "endDerivative": vector(8.26, 1.72) * mm});
            skFitSpline(sketch, "E122", {"points": [v(46.7, -31.26) * mm, v(45.31, -32.94) * mm, v(44.27, -35.06) * mm, v(43.88, -36.59) * mm], "startDerivative": vector(-4.19, -4.54) * mm, "endDerivative": vector(-1.04, -4.96) * mm});
            skFitSpline(sketch, "E123", {"points": [v(43.88, -36.59) * mm, v(45.8, -35.75) * mm], "startDerivative": vector(1.93, 0.84) * mm, "endDerivative": vector(1.93, 0.84) * mm});
            skFitSpline(sketch, "E124", {"points": [v(45.8, -35.75) * mm, v(47.24, -33.28) * mm, v(49.7, -31.26) * mm, v(52.52, -31.26) * mm], "startDerivative": vector(3.75, 7.58) * mm, "endDerivative": vector(8.86, -1.4) * mm});
            skFitSpline(sketch, "E125", {"points": [v(52.52, -31.26) * mm, v(50.45, -32.3) * mm, v(48.82, -33.87) * mm, v(48.27, -35) * mm], "startDerivative": vector(-5.78, -2.4) * mm, "endDerivative": vector(-1.5, -4.08) * mm});
            skFitSpline(sketch, "E126", {"points": [v(48.27, -35) * mm, v(50.45, -35) * mm], "startDerivative": vector(2.17, 0) * mm, "endDerivative": vector(2.17, 0) * mm});
            skFitSpline(sketch, "E127", {"points": [v(50.45, -35) * mm, v(51.56, -33.48) * mm, v(53.56, -31.9) * mm, v(55.43, -31.8) * mm], "startDerivative": vector(3.07, 4.7) * mm, "endDerivative": vector(5.94, -0.64) * mm});
            skFitSpline(sketch, "E128", {"points": [v(55.43, -31.8) * mm, v(54.05, -32.89) * mm, v(53.01, -34.07) * mm, v(52.52, -35) * mm], "startDerivative": vector(-3.89, -2.82) * mm, "endDerivative": vector(-1.48, -3.23) * mm});
            skFitSpline(sketch, "E129", {"points": [v(52.52, -35) * mm, v(54.05, -35) * mm], "startDerivative": vector(1.53, 0) * mm, "endDerivative": vector(1.53, 0) * mm});
            skFitSpline(sketch, "E130", {"points": [v(54.05, -35) * mm, v(55.93, -33.97) * mm, v(57.9, -33.82) * mm, v(58.99, -34.22) * mm], "startDerivative": vector(4.8, 3.3) * mm, "endDerivative": vector(3.6, -1.75) * mm});
            skFitSpline(sketch, "E131", {"points": [v(58.99, -34.22) * mm, v(57.11, -34.7) * mm, v(56.37, -35) * mm], "startDerivative": vector(-3.45, -0.8) * mm, "endDerivative": vector(-1.66, -0.78) * mm});
            skFitSpline(sketch, "E132", {"points": [v(56.37, -35) * mm, v(57.76, -36.31) * mm, v(58.99, -37.38) * mm, v(59.48, -38.91) * mm], "startDerivative": vector(3.82, -3.92) * mm, "endDerivative": vector(0.94, -5.15) * mm});
            skFitSpline(sketch, "E133", {"points": [v(59.48, -38.91) * mm, v(56.77, -37.48) * mm, v(53.6, -36.74) * mm, v(49.76, -36.98) * mm, v(46.15, -37.78) * mm, v(41.8, -39.65) * mm], "startDerivative": vector(-14.54, 8.57) * mm, "endDerivative": vector(-19.63, -9.4) * mm});
            skFitSpline(sketch, "E134", {"points": [v(41.8, -39.65) * mm, v(41.76, -40.44) * mm, v(41.16, -41.38) * mm, v(40.27, -41.23) * mm, v(39.68, -40.99) * mm, v(38.6, -41.03) * mm, v(38.15, -40.24) * mm, v(38.7, -38.91) * mm, v(38.84, -38.17) * mm, v(39.78, -37.63) * mm, v(40.77, -37.97) * mm, v(41.16, -37.73) * mm], "startDerivative": vector(0.4, -8.61) * mm, "endDerivative": vector(5.3, 5.88) * mm});
            skFitSpline(sketch, "E135", {"points": [v(41.16, -48.05) * mm, v(43.75, -46.72) * mm, v(47, -45.96) * mm, v(50.15, -45.96) * mm, v(53.04, -47.47) * mm], "startDerivative": vector(10.34, 6.13) * mm, "endDerivative": vector(11.07, -7.4) * mm});
            skFitSpline(sketch, "E136", {"points": [v(41.16, -48.05) * mm, v(40.47, -49.2) * mm, v(39.09, -49.25) * mm, v(38.16, -49.25) * mm, v(37.8, -48.4) * mm, v(38.38, -47.56) * mm, v(38.78, -46.85) * mm, v(39.78, -46.5) * mm, v(40.29, -46.85) * mm], "startDerivative": vector(-3.49, -10.12) * mm, "endDerivative": vector(4.22, -4.81) * mm});
            skFitSpline(sketch, "E137", {"points": [v(40.29, -46.85) * mm, v(40.29, -45.12) * mm, v(41.16, -43.12) * mm, v(43.18, -41.74) * mm], "startDerivative": vector(-0.46, 5.56) * mm, "endDerivative": vector(6.26, 3.26) * mm});
            skFitSpline(sketch, "E138", {"points": [v(43.18, -41.74) * mm, v(41.99, -43.92) * mm, v(41.99, -46) * mm], "startDerivative": vector(-2.87, -4.13) * mm, "endDerivative": vector(0.54, -4.4) * mm});
            skFitSpline(sketch, "E139", {"points": [v(41.99, -46) * mm, v(42.69, -45.6) * mm], "startDerivative": vector(0.7, 0.4) * mm, "endDerivative": vector(0.7, 0.4) * mm});
            skFitSpline(sketch, "E140", {"points": [v(42.69, -45.6) * mm, v(43.53, -43.87) * mm, v(45.41, -42.05) * mm, v(46.84, -41.66) * mm], "startDerivative": vector(1.97, 5.18) * mm, "endDerivative": vector(4.82, 0.6) * mm});
            skFitSpline(sketch, "E141", {"points": [v(46.84, -41.66) * mm, v(45.22, -43.06) * mm, v(44.57, -44.8) * mm], "startDerivative": vector(-3.6, -2.46) * mm, "endDerivative": vector(-0.91, -3.85) * mm});
            skFitSpline(sketch, "E142", {"points": [v(44.57, -44.8) * mm, v(45.77, -44.8) * mm], "startDerivative": vector(1.2, 0) * mm, "endDerivative": vector(1.2, 0) * mm});
            skFitSpline(sketch, "E143", {"points": [v(45.77, -44.8) * mm, v(46.84, -42.93) * mm, v(49.7, -42.05) * mm], "startDerivative": vector(1.65, 4.66) * mm, "endDerivative": vector(6.09, 0.96) * mm});
            skFitSpline(sketch, "E144", {"points": [v(49.7, -42.05) * mm, v(48.5, -43) * mm, v(47.75, -44.03) * mm], "startDerivative": vector(-2.5, -1.7) * mm, "endDerivative": vector(-1.39, -2.26) * mm});
            skFitSpline(sketch, "E145", {"points": [v(47.75, -44.03) * mm, v(48.83, -44.03) * mm], "startDerivative": vector(1.08, 0) * mm, "endDerivative": vector(1.08, 0) * mm});
            skFitSpline(sketch, "E146", {"points": [v(48.83, -44.03) * mm, v(49.92, -43.35) * mm, v(51.4, -43.3) * mm], "startDerivative": vector(2.12, 1.72) * mm, "endDerivative": vector(3.02, -0.25) * mm});
            skFitSpline(sketch, "E147", {"points": [v(51.4, -43.3) * mm, v(50.45, -44.03) * mm, v(50.2, -44.33) * mm], "startDerivative": vector(-1.75, -1.24) * mm, "endDerivative": vector(-0.56, -0.76) * mm});
            skFitSpline(sketch, "E148", {"points": [v(50.2, -44.33) * mm, v(51.4, -45.23) * mm, v(52.68, -46.63) * mm, v(53.04, -47.47) * mm], "startDerivative": vector(3.4, -2.34) * mm, "endDerivative": vector(0.89, -2.99) * mm});
            skLineSegment(sketch, "E149", {"start": v(-7.77, 48.7) * mm, "end": v(-7.05, 40.2) * mm});
            skLineSegment(sketch, "E150", {"start": v(-7.05, 40.2) * mm, "end": v(-5, 40.64) * mm});
            skLineSegment(sketch, "E151", {"start": v(-5, 40.64) * mm, "end": v(-5.27, 43.94) * mm});
            skFitSpline(sketch, "E152", {"points": [v(-5.27, 43.94) * mm, v(-2.26, 44.65) * mm, v(0.48, 45.3) * mm, v(2.15, 46.28) * mm, v(2.67, 48.06) * mm, v(2.05, 50.03) * mm, v(0.76, 50.68) * mm, v(-2.47, 50.06) * mm, v(-5.27, 49.45) * mm, v(-7.77, 48.7) * mm], "startDerivative": vector(23.92, 5.85) * mm, "endDerivative": vector(-21.48, -6.92) * mm});
            skFitSpline(sketch, "E153", {"points": [v(6.85, 49.34) * mm, v(8.94, 49.77) * mm, v(11.73, 50.14) * mm, v(12.85, 50.1) * mm, v(13.07, 48.7) * mm, v(13.07, 46.6) * mm, v(11.57, 46.23) * mm, v(8.03, 45.86) * mm, v(6.74, 45.7) * mm, v(6.37, 47.09) * mm, v(6.1, 48.7) * mm, v(6.85, 49.34) * mm]});
            skFitSpline(sketch, "E154", {"points": [v(5.09, 51.46) * mm, v(12.22, 52.58) * mm, v(14.4, 52.47) * mm, v(15.2, 50.07) * mm, v(15.25, 45.92) * mm, v(14.4, 44.6) * mm, v(11, 43.94) * mm, v(7.06, 43.37) * mm, v(4.93, 43.42) * mm, v(4.23, 44.86) * mm, v(3.97, 48.32) * mm, v(3.97, 50.23) * mm, v(5.09, 51.46) * mm]});
            skLineSegment(sketch, "E155", {"start": v(17.18, 44.77) * mm, "end": v(16.62, 52.94) * mm});
            skFitSpline(sketch, "E156", {"points": [v(16.62, 52.94) * mm, v(25.85, 53.69) * mm], "startDerivative": vector(9.23, 0.75) * mm, "endDerivative": vector(9.23, 0.75) * mm});
            skFitSpline(sketch, "E157", {"points": [v(25.85, 53.69) * mm, v(27.16, 53.3) * mm, v(27.84, 52.33) * mm, v(27.84, 51.26) * mm, v(27.64, 50.24) * mm, v(27.2, 49.56) * mm], "startDerivative": vector(6.3, -0.93) * mm, "endDerivative": vector(-2.9, -3.64) * mm});
            skFitSpline(sketch, "E158", {"points": [v(27.2, 49.56) * mm, v(28.08, 48.68) * mm, v(28.23, 47.36) * mm, v(28.13, 45.46) * mm], "startDerivative": vector(3.45, -2.58) * mm, "endDerivative": vector(-0.29, -5.17) * mm});
            skLineSegment(sketch, "E159", {"start": v(17.18, 44.77) * mm, "end": v(19.17, 44.9) * mm});
            skLineSegment(sketch, "E160", {"start": v(19.17, 44.9) * mm, "end": v(18.96, 47.94) * mm});
            skLineSegment(sketch, "E161", {"start": v(28.13, 45.46) * mm, "end": v(26.35, 45.46) * mm});
            skFitSpline(sketch, "E162", {"points": [v(18.96, 47.94) * mm, v(23.88, 48.38) * mm, v(25.65, 48.38) * mm, v(26.04, 47.94) * mm, v(26.16, 46.18) * mm, v(26.35, 45.46) * mm], "startDerivative": vector(15.82, 1.44) * mm, "endDerivative": vector(1.81, -4.43) * mm});
            skLineSegment(sketch, "E163", {"start": v(55.35, 52.15) * mm, "end": v(54.78, 44.26) * mm});
            skLineSegment(sketch, "E164", {"start": v(54.78, 44.26) * mm, "end": v(56.9, 43.69) * mm});
            skLineSegment(sketch, "E165", {"start": v(56.9, 43.69) * mm, "end": v(56.9, 46.65) * mm});
            skLineSegment(sketch, "E166", {"start": v(56.9, 46.65) * mm, "end": v(63.76, 45.66) * mm});
            skLineSegment(sketch, "E167", {"start": v(63.76, 45.66) * mm, "end": v(63.76, 42.44) * mm});
            skLineSegment(sketch, "E168", {"start": v(63.76, 42.44) * mm, "end": v(65.84, 41.97) * mm});
            skLineSegment(sketch, "E169", {"start": v(65.84, 41.97) * mm, "end": v(66.46, 50.54) * mm});
            skLineSegment(sketch, "E170", {"start": v(66.46, 50.54) * mm, "end": v(64.33, 51.06) * mm});
            skLineSegment(sketch, "E171", {"start": v(55.35, 52.15) * mm, "end": v(57.53, 52) * mm});
            skLineSegment(sketch, "E172", {"start": v(57.53, 52) * mm, "end": v(57.53, 48.77) * mm});
            skLineSegment(sketch, "E173", {"start": v(57.53, 48.77) * mm, "end": v(63.97, 47.79) * mm});
            skLineSegment(sketch, "E174", {"start": v(63.97, 47.79) * mm, "end": v(64.33, 51.06) * mm});
            skLineSegment(sketch, "E175", {"start": v(67.44, 41.66) * mm, "end": v(75.84, 39.6) * mm});
            skLineSegment(sketch, "E176", {"start": v(75.84, 39.6) * mm, "end": v(76.17, 41.44) * mm});
            skLineSegment(sketch, "E177", {"start": v(76.17, 41.44) * mm, "end": v(69.82, 43.12) * mm});
            skLineSegment(sketch, "E178", {"start": v(69.82, 43.12) * mm, "end": v(69.82, 44.42) * mm});
            skLineSegment(sketch, "E179", {"start": v(69.82, 44.42) * mm, "end": v(76.22, 42.85) * mm});
            skLineSegment(sketch, "E180", {"start": v(76.22, 42.85) * mm, "end": v(76.44, 44.7) * mm});
            skLineSegment(sketch, "E181", {"start": v(76.44, 44.7) * mm, "end": v(70.2, 46.26) * mm});
            skLineSegment(sketch, "E182", {"start": v(70.2, 46.26) * mm, "end": v(70.2, 47.4) * mm});
            skLineSegment(sketch, "E183", {"start": v(70.2, 47.4) * mm, "end": v(76.76, 46.05) * mm});
            skLineSegment(sketch, "E184", {"start": v(76.76, 46.05) * mm, "end": v(76.92, 48) * mm});
            skLineSegment(sketch, "E185", {"start": v(76.92, 48) * mm, "end": v(68.2, 50.22) * mm});
            skLineSegment(sketch, "E186", {"start": v(68.2, 50.22) * mm, "end": v(67.44, 41.66) * mm});
            skFitSpline(sketch, "E187", {"points": [v(29.94, 45.6) * mm, v(32.69, 45.58) * mm, v(37.23, 45.51) * mm, v(39.88, 45.51) * mm, v(40.93, 46.29) * mm, v(41.25, 48.48) * mm, v(40.7, 50.17) * mm, v(38.42, 50.58) * mm, v(34.36, 50.49) * mm, v(31.82, 50.67) * mm, v(31.8, 51.22) * mm, v(34.04, 51.5) * mm, v(38.37, 51.54) * mm, v(41.2, 51.5) * mm], "startDerivative": vector(31.33, 11.8) * mm, "endDerivative": vector(32.68, -0.9) * mm});
            skLineSegment(sketch, "E188", {"start": v(29.94, 45.6) * mm, "end": v(29.94, 47.55) * mm});
            skLineSegment(sketch, "E189", {"start": v(41.2, 51.5) * mm, "end": v(41.2, 53.74) * mm});
            skFitSpline(sketch, "E190", {"points": [v(41.2, 53.74) * mm, v(36.31, 53.74) * mm, v(31.4, 53.74) * mm, v(29.87, 53.09) * mm, v(29.26, 51.19) * mm, v(30.1, 49) * mm, v(33.44, 48.54) * mm, v(36.4, 48.6) * mm, v(38.03, 48.54) * mm, v(38.58, 48.17) * mm, v(38.07, 47.76) * mm, v(36.36, 47.57) * mm, v(33.85, 47.57) * mm, v(29.94, 47.55) * mm], "startDerivative": vector(-42.62, -0.56) * mm, "endDerivative": vector(-41.65, -0.27) * mm});
            skLineSegment(sketch, "E191", {"start": v(53.55, 52.6) * mm, "end": v(53.55, 50.5) * mm});
            skLineSegment(sketch, "E192", {"start": v(53.28, 46.49) * mm, "end": v(53.2, 44.52) * mm});
            skPoint(sketch, "E193.2.internal.snap0", {"position": v(53.24, 45.5) * mm});
            skFitSpline(sketch, "E193", {"points": [v(53.2, 44.52) * mm, v(45.97, 45.06) * mm, v(43.25, 45.5) * mm, v(42.49, 46.8) * mm, v(42.44, 50.23) * mm, v(42.67, 52.29) * mm, v(43.96, 53.5) * mm, v(47.12, 53.37) * mm, v(50.12, 53.08) * mm, v(53.55, 52.6) * mm], "startDerivative": vector(-45.82, 3.66) * mm, "endDerivative": vector(28.86, -7.43) * mm});
            skFitSpline(sketch, "E194", {"points": [v(53.55, 50.5) * mm, v(49.92, 50.86) * mm, v(47.12, 51.18) * mm, v(45.37, 51.06) * mm, v(44.78, 49.75) * mm, v(45.16, 47.7) * mm, v(47.9, 47.12) * mm, v(51.73, 46.74) * mm, v(53.28, 46.49) * mm], "startDerivative": vector(-24.78, 2.57) * mm, "endDerivative": vector(13.92, -2.35) * mm});
            skLineSegment(sketch, "E195", {"start": v(-5.72, 45.89) * mm, "end": v(-5.72, 47.04) * mm});
            skFitSpline(sketch, "E196", {"points": [v(-5.72, 47.04) * mm, v(-0.7, 48.2) * mm, v(0.45, 48.36) * mm, v(0.56, 47.73) * mm, v(-1.28, 47.04) * mm, v(-3.99, 46.35) * mm, v(-5.72, 45.89) * mm], "startDerivative": vector(21.81, 4.5) * mm, "endDerivative": vector(-10.46, -2.76) * mm});
            skFitSpline(sketch, "E197", {"points": [v(19.08, 50.05) * mm, v(19.08, 51.23) * mm], "startDerivative": vector(0, 1.17) * mm, "endDerivative": vector(0, 1.17) * mm});
            skFitSpline(sketch, "E198", {"points": [v(19.08, 51.23) * mm, v(23.18, 51.64) * mm, v(24.95, 51.67) * mm, v(25.45, 51.23) * mm, v(25.16, 50.64) * mm, v(22.86, 50.29) * mm, v(20.48, 50.18) * mm, v(19.08, 50.05) * mm], "startDerivative": vector(20.47, 1.99) * mm, "endDerivative": vector(-10.5, -0.9) * mm});
            skText(sketch, "E199", { "text": "STUTTGART", "fontName": "OpenSans-Regular.ttf"});
            const initialGuessF0  = {"E199": [0.0193, 0.01176, 1, 0, 0.004]};
            skSetInitialGuess(sketch, initialGuessF0);
            skSolve(sketch);
        }
        {
            var Q0;
            Q0=makeQuery(id+"F0.imprint","IMPRINT",FACE,{"disambiguationData":[TD([[makeQuery(id+"F0.imprint","IMPRINT",EDGE,{"derivedFrom":sQuery(id+"F0.wireOp",EDGE,"E57")}),-1.0]])]});
            var Q1;
            Q1=makeQuery(id+"F0.imprint","IMPRINT",FACE,{"disambiguationData":[TD([[makeQuery(id+"F0.imprint","IMPRINT",EDGE,{"derivedFrom":sQuery(id+"F0.wireOp",EDGE,"E199.sketch_text.stroke-91")}),1.0]])]});
            var Q2;
            Q2=makeQuery(id+"F0.imprint","IMPRINT",FACE,{"disambiguationData":[TD([[makeQuery(id+"F0.imprint","IMPRINT",EDGE,{"derivedFrom":sQuery(id+"F0.wireOp",EDGE,"E199.sketch_text.stroke-107")}),1.0]])]});
            extrude(context, id + "F1", {"entities" : qUnion([Q0, Q1, Q2]), "depth" : 12.95 * mm});
        }
        {
            var Q0;
            Q0=makeQuery(id+"F0.imprint","IMPRINT",FACE,{"disambiguationData":[TD([[makeQuery(id+"F0.imprint","IMPRINT",EDGE,{"derivedFrom":sQuery(id+"F0.wireOp",EDGE,"E6.0")}),1.0]])]});
            var Q1;
            Q1=makeQuery(id+"F0.imprint","IMPRINT",FACE,{"disambiguationData":[TD([[makeQuery(id+"F0.imprint","IMPRINT",EDGE,{"derivedFrom":sQuery(id+"F0.wireOp",EDGE,"E19")}),-1.0]])]});
            var Q2;
            Q2=makeQuery(id+"F0.imprint","IMPRINT",FACE,{"disambiguationData":[TD([[makeQuery(id+"F0.imprint","IMPRINT",EDGE,{"derivedFrom":sQuery(id+"F0.wireOp",EDGE,"E121")}),-1.0]])]});
            var Q3;
            Q3=makeQuery(id+"F0.imprint","IMPRINT",FACE,{"disambiguationData":[TD([[makeQuery(id+"F0.imprint","IMPRINT",EDGE,{"derivedFrom":sQuery(id+"F0.wireOp",EDGE,"E135")}),1.0]])]});
            extrude(context, id + "F2", {"entities" : qUnion([Q0, Q1, Q2, Q3]), "operationType" : NewBodyOperationType.ADD, "depth" : 12.95 * mm});
        }
        {
            var Q0;
            Q0=makeQuery(id+"F0.imprint","IMPRINT",FACE,{"disambiguationData":[TD([[makeQuery(id+"F0.imprint","IMPRINT",EDGE,{"derivedFrom":sQuery(id+"F0.wireOp",EDGE,"E0")}),-1.0]])]});
            extrude(context, id + "F3", {"entities" : qUnion([Q0]), "depth" : 12.95 * mm});
        }
        {
            var Q0;
            Q0=makeQuery(id+"F0.imprint","IMPRINT",FACE,{"disambiguationData":[TD([[makeQuery(id+"F0.imprint","IMPRINT",EDGE,{"derivedFrom":sQuery(id+"F0.wireOp",EDGE,"E153")}),1.0]])]});
            var Q1;
            Q1=makeQuery(id+"F0.imprint","IMPRINT",FACE,{"disambiguationData":[TD([[makeQuery(id+"F0.imprint","IMPRINT",EDGE,{"derivedFrom":sQuery(id+"F0.wireOp",EDGE,"E149")}),1.0]])]});
            var Q2;
            Q2=makeQuery(id+"F0.imprint","IMPRINT",FACE,{"disambiguationData":[TD([[makeQuery(id+"F0.imprint","IMPRINT",EDGE,{"derivedFrom":sQuery(id+"F0.wireOp",EDGE,"E155")}),-1.0]])]});
            var Q3;
            Q3=makeQuery(id+"F0.imprint","IMPRINT",FACE,{"disambiguationData":[TD([[makeQuery(id+"F0.imprint","IMPRINT",EDGE,{"derivedFrom":sQuery(id+"F0.wireOp",EDGE,"E187")}),1.0]])]});
            var Q4;
            Q4=makeQuery(id+"F0.imprint","IMPRINT",FACE,{"disambiguationData":[TD([[makeQuery(id+"F0.imprint","IMPRINT",EDGE,{"derivedFrom":sQuery(id+"F0.wireOp",EDGE,"E191")}),-1.0]])]});
            var Q5;
            Q5=makeQuery(id+"F0.imprint","IMPRINT",FACE,{"disambiguationData":[TD([[makeQuery(id+"F0.imprint","IMPRINT",EDGE,{"derivedFrom":sQuery(id+"F0.wireOp",EDGE,"E163")}),1.0]])]});
            var Q6;
            Q6=makeQuery(id+"F0.imprint","IMPRINT",FACE,{"disambiguationData":[TD([[makeQuery(id+"F0.imprint","IMPRINT",EDGE,{"derivedFrom":sQuery(id+"F0.wireOp",EDGE,"E175")}),1.0]])]});
            extrude(context, id + "F4", {"entities" : qUnion([Q0, Q1, Q2, Q3, Q4, Q5, Q6]), "depth" : 12.95 * mm});
        }
    });
